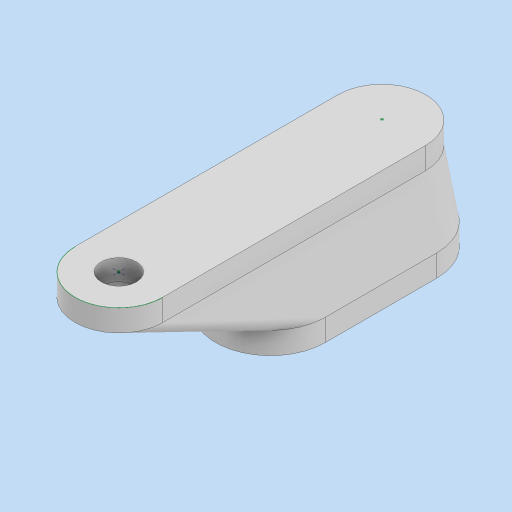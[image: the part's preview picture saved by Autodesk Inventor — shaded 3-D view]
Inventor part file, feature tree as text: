
AUTODESK INVENTOR PART (.ipt)
format: ipt  version: 2024 (Build 280153000, 153)  size: 300,032 bytes
history: native  units: in
note: dims shown in document units (in); Inventor stores cm internally (conversion verified against a paired STEP export)
features: sketch x5, extrude x3, plane x2, loft x1, sweep x1, other x1
ambient origin geometry x8: Origin, YZ Plane, XZ Plane, XY Plane, X Axis, Y Axis, Z Axis, Center Point
bodies: Solid1 (feature_tree)
feature tree (13):
  sketch  "Sketch1"  dims[d0=0.2638in d1=0.1575in]
  plane  "Work Plane1"
  sketch  "Sketch2"  dims[d4=0.0394in d5=0.1181in]
  extrude  "Extrusion1"  Depth=0.1575in
  extrude  "Extrusion2"  Depth=0.1181in
  loft  "Loft2"
  plane  "Work Plane3"
  sketch  "Sketch7"  dims[d18=0.2638in d19=0.8465in]
  sweep  "Sweep2"
  extrude  "Extrusion3"  Depth=0.5in
  other  "Edges2"
  sketch  "Sketch8"  dims[d20=2.3622in d22=0.0787in d23=0.3937in d25=1.0in d27=0.0157in]
  sketch  "Sketch9"  dims[d28=0.625in d29=0.5in d30=1.5in d31=0.5in d32=0.125in d33=0.0in d38=0.125in d39=0.0in d49=0.0in d50=90.0deg d51=0.0in d52=90.0deg d62=0.2in d63=0.0069in d64=0.0in d65=0.25in d66=0.0in]
